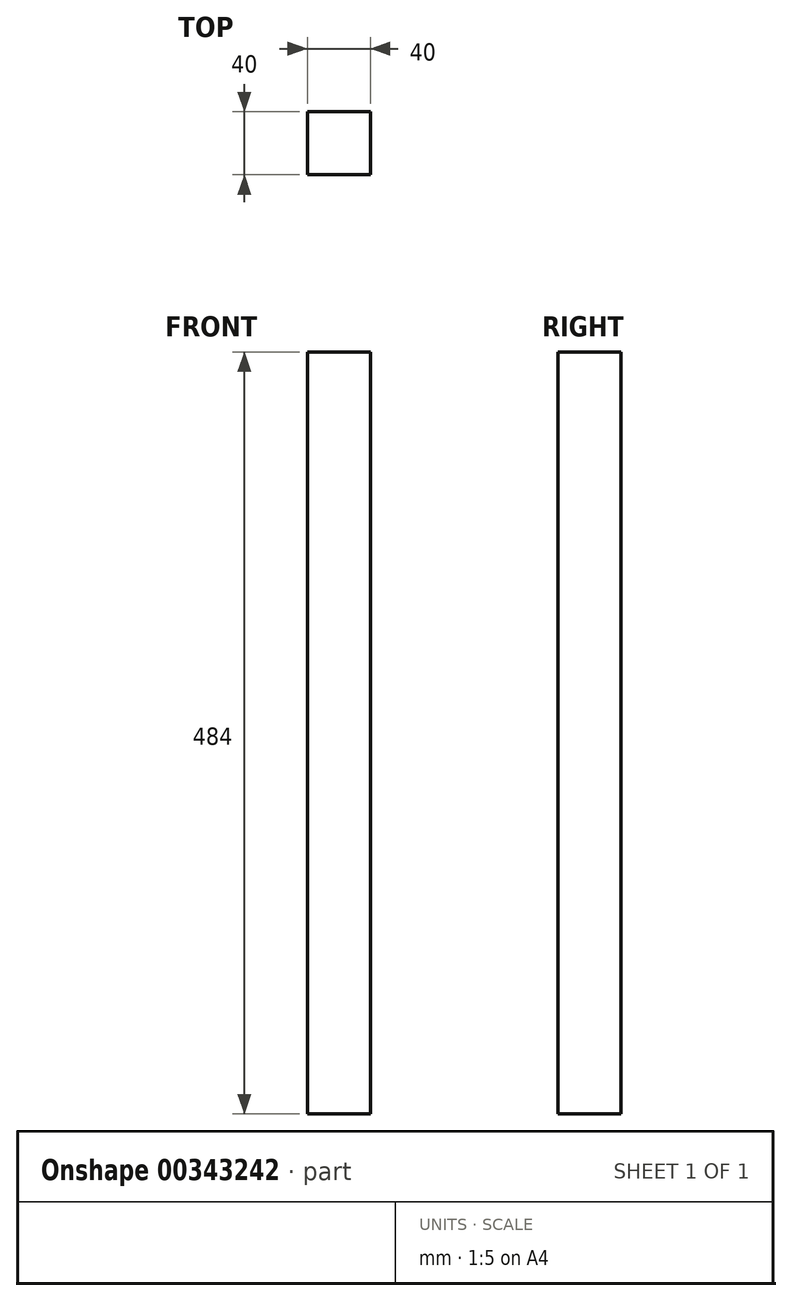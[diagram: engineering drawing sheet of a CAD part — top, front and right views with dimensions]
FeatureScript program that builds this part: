
annotation { "Feature Type Name" : "Feature", "Feature Type Description" : "" }
export const myFeature = defineFeature(function(context is Context, id is Id, definition is map)
    precondition{}
    {
        {
            var Q0;
            Q0=qCreatedBy(makeId("Front.planeOp"),FACE);
            var sketch = newSketch(context, id + "F0", { "sketchPlane" : qUnion([Q0])});
            skLineSegment(sketch, "E0.bottom", {"start": v(20, 242) * mm, "end": v(-20, 242) * mm});
            skLineSegment(sketch, "E0.top", {"start": v(20, -242) * mm, "end": v(-20, -242) * mm});
            skLineSegment(sketch, "E0.left", {"start": v(20, 242) * mm, "end": v(20, -242) * mm});
            skLineSegment(sketch, "E0.right", {"start": v(-20, 242) * mm, "end": v(-20, -242) * mm});
            skPoint(sketch, "E0.middle", {"position": v(0, 0) * mm});
            skSolve(sketch);
        }
        {
            var Q0;
            Q0=makeQuery(id+"F0.imprint","IMPRINT",FACE,{"disambiguationData":[TD([[makeQuery(id+"F0.imprint","IMPRINT",EDGE,{"derivedFrom":sQuery(id+"F0.wireOp",EDGE,"E0.bottom")}),1.0]])]});
            extrude(context, id + "F1", {"entities" : qUnion([Q0]), "depth" : 40 * mm});
        }
    });
